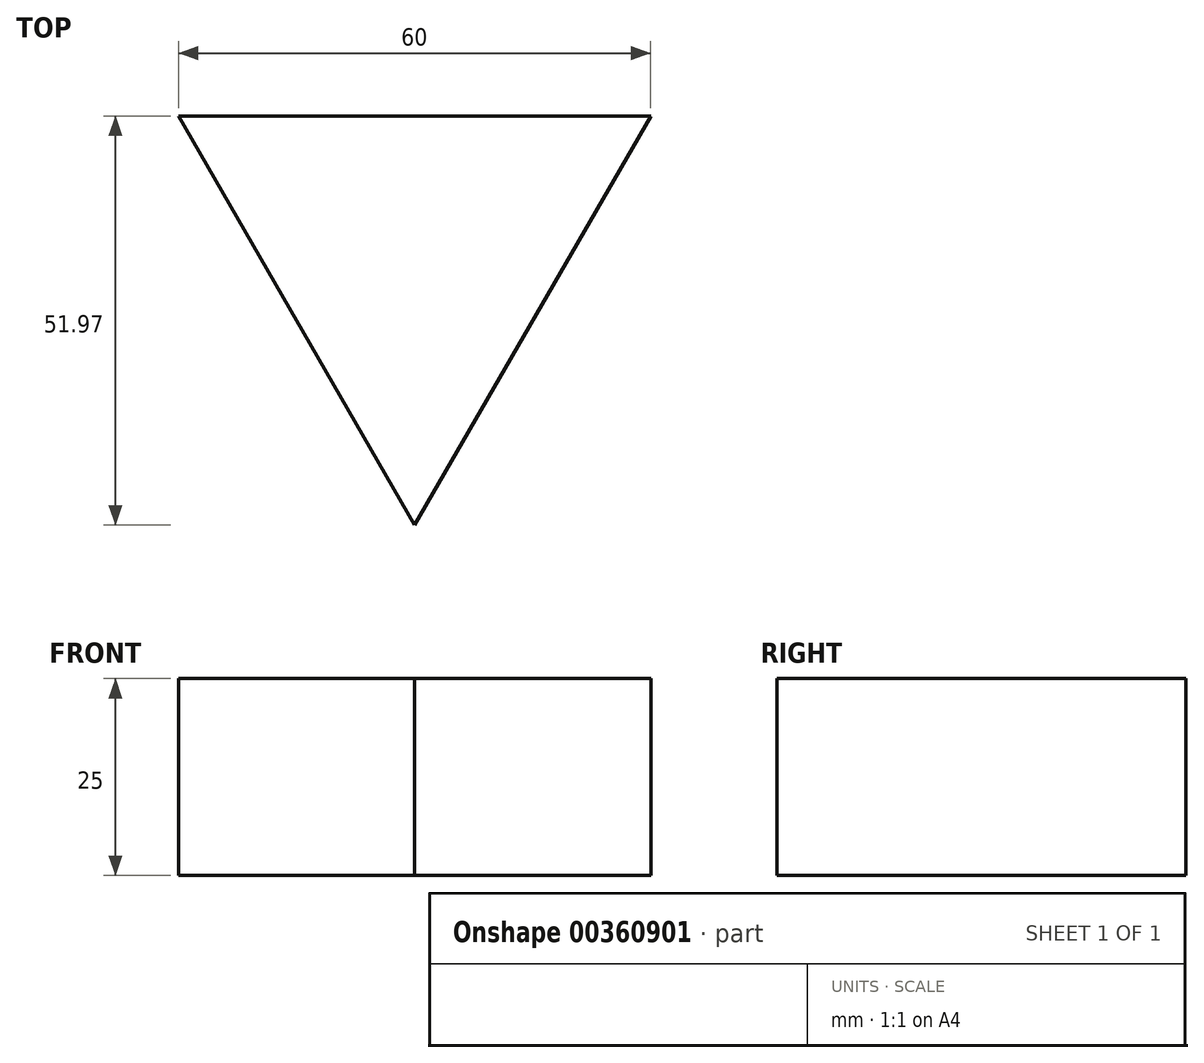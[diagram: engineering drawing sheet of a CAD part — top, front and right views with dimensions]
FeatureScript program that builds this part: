
annotation { "Feature Type Name" : "Feature", "Feature Type Description" : "" }
export const myFeature = defineFeature(function(context is Context, id is Id, definition is map)
    precondition{}
    {
        {
            var Q0;
            Q0=qCreatedBy(makeId("Top.planeOp"),FACE);
            var sketch = newSketch(context, id + "F0", { "sketchPlane" : qUnion([Q0])});
            skLineSegment(sketch, "E0", {"start": v(-30.97, 50.25) * mm, "end": v(29.03, 50.25) * mm});
            skLineSegment(sketch, "E1", {"start": v(29.03, 50.25) * mm, "end": v(-0.97, -1.72) * mm});
            skLineSegment(sketch, "E2", {"start": v(-0.97, -1.72) * mm, "end": v(-30.97, 50.25) * mm});
            skPoint(sketch, "E3.end.orphan", {"position": v(-0.97, 8.41) * mm});
            skPoint(sketch, "E3.start.orphan", {"position": v(-0.97, 50.25) * mm});
            skLineSegment(sketch, "E4", {"start": v(66.88, -16.48) * mm, "end": v(166.88, -16.48) * mm});
            skLineSegment(sketch, "E5", {"start": v(66.88, -16.48) * mm, "end": v(86.88, 33.52) * mm});
            skLineSegment(sketch, "E6", {"start": v(86.88, 33.52) * mm, "end": v(146.88, 33.52) * mm});
            skLineSegment(sketch, "E7", {"start": v(166.88, -16.48) * mm, "end": v(146.88, 33.52) * mm});
            skPoint(sketch, "E8.start.orphan", {"position": v(166.88, 33.52) * mm});
            skPoint(sketch, "E9.start.orphan", {"position": v(66.88, 33.52) * mm});
            skLineSegment(sketch, "E10", {"start": v(-98.23, -101.19) * mm, "end": v(-18.23, -101.19) * mm});
            skLineSegment(sketch, "E11", {"start": v(-18.23, -101.19) * mm, "end": v(11.77, -49.23) * mm});
            skLineSegment(sketch, "E12", {"start": v(-98.23, -101.19) * mm, "end": v(-74.3, -35.41) * mm});
            skLineSegment(sketch, "E13", {"start": v(-74.3, -35.41) * mm, "end": v(-49.57, -48.56) * mm});
            skSolve(sketch);
        }
        {
            var Q0;
            Q0=makeQuery(id+"F0.imprint","IMPRINT",FACE,{"disambiguationData":[TD([[makeQuery(id+"F0.imprint","IMPRINT",EDGE,{"derivedFrom":sQuery(id+"F0.wireOp",EDGE,"E0")}),-1.0]])]});
            extrude(context, id + "F1", {"entities" : qUnion([Q0]), "depth" : 25 * mm});
        }
    });
